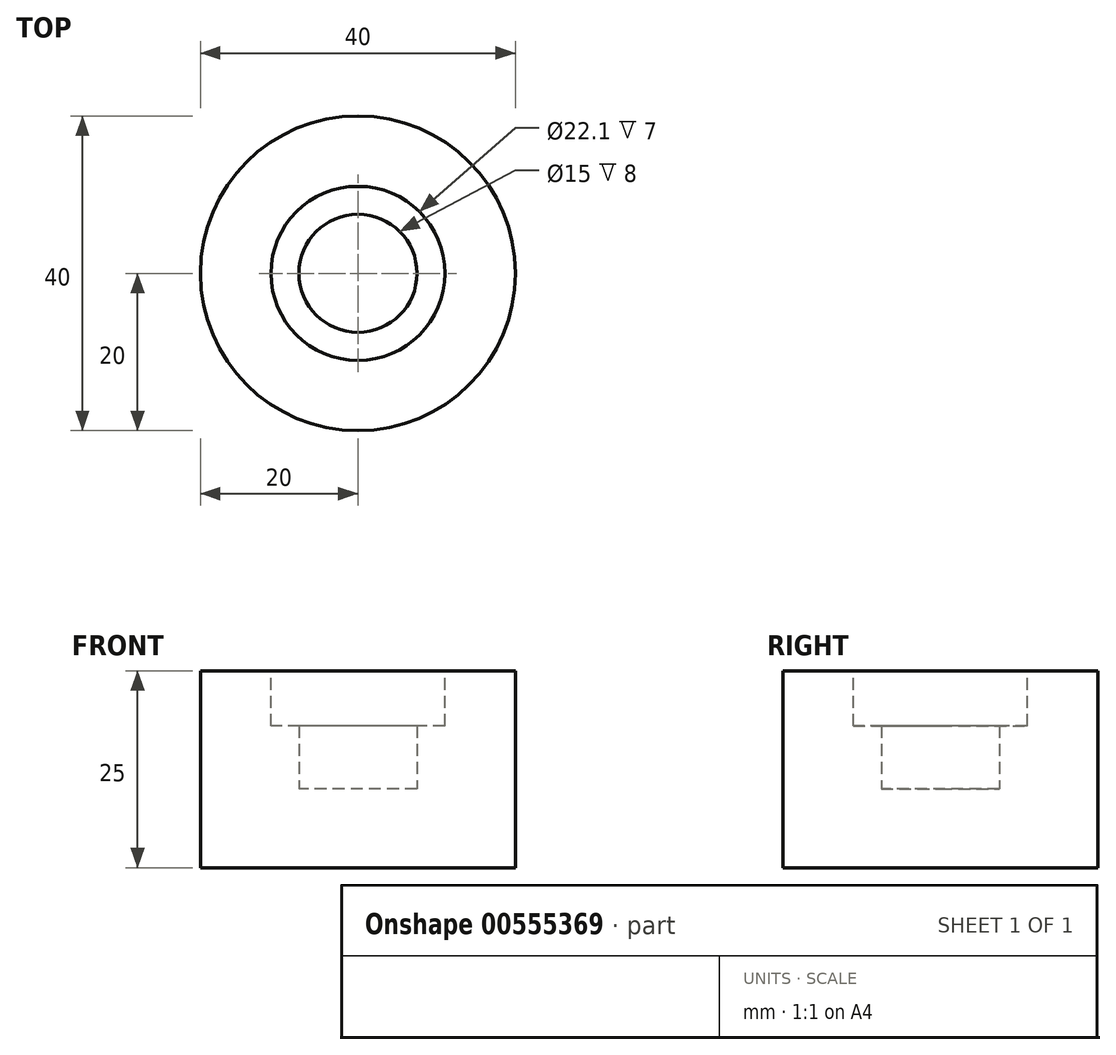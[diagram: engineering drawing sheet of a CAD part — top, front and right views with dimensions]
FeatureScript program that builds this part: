
annotation { "Feature Type Name" : "Feature", "Feature Type Description" : "" }
export const myFeature = defineFeature(function(context is Context, id is Id, definition is map)
    precondition{}
    {
        {
            var Q0;
            Q0=qCreatedBy(makeId("Top.planeOp"),FACE);
            var sketch = newSketch(context, id + "F0", { "sketchPlane" : qUnion([Q0])});
            skCircle(sketch, "E0", {"center": v(0, 0) * mm, "radius": 20 * mm});
            skSolve(sketch);
        }
        {
            var Q0;
            Q0=makeQuery(id+"F0.imprint","IMPRINT",FACE,{"disambiguationData":[TD([[makeQuery(id+"F0.imprint","IMPRINT",EDGE,{"derivedFrom":sQuery(id+"F0.wireOp",EDGE,"E0")}),1.0]])]});
            extrude(context, id + "F1", {"entities" : qUnion([Q0]), "depth" : 25 * mm, "offsetDistance" : 25 * mm});
        }
        {
            var Q0;
            Q0=makeQuery(id+"F1.opExtrude","CAP_FACE",FACE,{"disambiguationData":[OSD([sQuery(id+"F0.wireOp",EDGE,"E0")])],"isStart":false});
            var sketch = newSketch(context, id + "F2", { "sketchPlane" : qUnion([Q0])});
            skCircle(sketch, "E1", {"center": v(0, 0) * mm, "radius": 11.05 * mm});
            skSolve(sketch);
        }
        {
            var Q0;
            Q0=makeQuery(id+"F2.imprint","IMPRINT",FACE,{"disambiguationData":[TD([[makeQuery(id+"F2.imprint","IMPRINT",EDGE,{"derivedFrom":sQuery(id+"F2.wireOp",EDGE,"E1")}),1.0]])]});
            extrude(context, id + "F3", {"entities" : qUnion([Q0]), "operationType" : NewBodyOperationType.REMOVE, "oppositeDirection" : true, "depth" : 15 * mm, "offsetDistance" : 25 * mm});
        }
        {
            var Q0;
            Q0=makeQuery(id+"F3.boolean.opBoolean","COPY",FACE,{"derivedFrom":makeQuery(id+"F3.opExtrude","CAP_FACE",FACE,{"disambiguationData":[OSD([sQuery(id+"F2.wireOp",EDGE,"E1")])],"isStart":false})});
            var sketch = newSketch(context, id + "F4", { "sketchPlane" : qUnion([Q0])});
            skCircle(sketch, "E2", {"center": v(0, 0) * mm, "radius": 7.5 * mm});
            skSolve(sketch);
        }
        {
            var Q0;
            Q0=makeQuery(id+"F4.imprint","IMPRINT",FACE,{"disambiguationData":[TD([[makeQuery(id+"F4.imprint","IMPRINT",EDGE,{"derivedFrom":sQuery(id+"F4.wireOp",EDGE,"E2")}),-1.0]])]});
            extrude(context, id + "F5", {"entities" : qUnion([Q0]), "operationType" : NewBodyOperationType.ADD, "depth" : 8 * mm, "offsetDistance" : 25 * mm});
        }
    });
